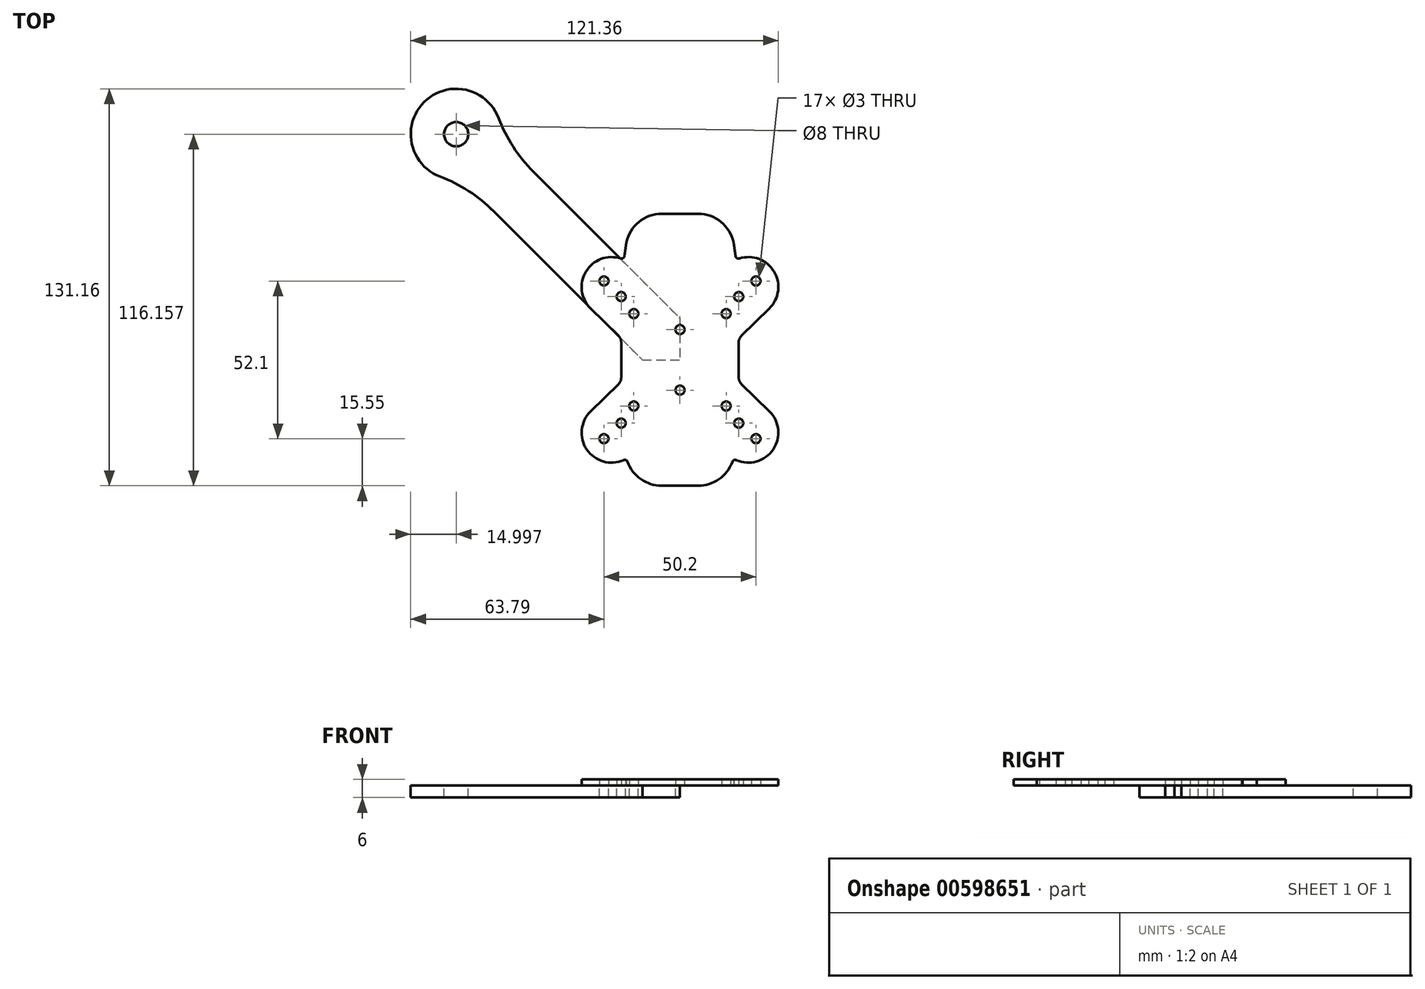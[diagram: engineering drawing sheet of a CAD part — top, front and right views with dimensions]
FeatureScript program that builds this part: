
annotation { "Feature Type Name" : "Feature", "Feature Type Description" : "" }
export const myFeature = defineFeature(function(context is Context, id is Id, definition is map)
    precondition{}
    {
        {
            var Q0;
            Q0=qCreatedBy(makeId("Top.planeOp"),FACE);
            var sketch = newSketch(context, id + "F0", { "sketchPlane" : qUnion([Q0])});
            skLineSegment(sketch, "E0", {"start": v(-6, 48.24) * mm, "end": v(6, 48.24) * mm});
            skLineSegment(sketch, "E1", {"start": v(-6, -41.6) * mm, "end": v(6, -41.6) * mm});
            skCircle(sketch, "E2", {"center": v(-25.1, 26.05) * mm, "radius": 1.5 * mm});
            skCircle(sketch, "E3", {"center": v(-19.4, 20.9) * mm, "radius": 1.5 * mm});
            skCircle(sketch, "E4", {"center": v(-15.25, 15.25) * mm, "radius": 1.5 * mm});
            skCircle(sketch, "E5", {"center": v(0, 10) * mm, "radius": 1.5 * mm});
            skLineSegment(sketch, "E6", {"start": v(-19.4, 5.82) * mm, "end": v(-19.4, -5.82) * mm});
            skCircle(sketch, "E7.MirrorC", {"center": v(-25.1, -26.05) * mm, "radius": 1.5 * mm});
            skCircle(sketch, "E8.MirrorC", {"center": v(-15.25, -15.25) * mm, "radius": 1.5 * mm});
            skCircle(sketch, "E9.MirrorC", {"center": v(-19.4, -20.9) * mm, "radius": 1.5 * mm});
            skCircle(sketch, "E10.MirrorC", {"center": v(0, -10) * mm, "radius": 1.5 * mm});
            skCircle(sketch, "E11.MirrorC", {"center": v(25.1, 26.05) * mm, "radius": 1.5 * mm});
            skCircle(sketch, "E12.MirrorC", {"center": v(19.4, 20.9) * mm, "radius": 1.5 * mm});
            skCircle(sketch, "E13.MirrorC", {"center": v(15.25, 15.25) * mm, "radius": 1.5 * mm});
            skCircle(sketch, "E14.MirrorC", {"center": v(19.4, -20.9) * mm, "radius": 1.5 * mm});
            skCircle(sketch, "E15.MirrorC", {"center": v(15.25, -15.25) * mm, "radius": 1.5 * mm});
            skCircle(sketch, "E16.MirrorC", {"center": v(25.1, -26.05) * mm, "radius": 1.5 * mm});
            skLineSegment(sketch, "E17.MirrorCS", {"start": v(19.4, 5.82) * mm, "end": v(19.4, -5.82) * mm});
            skArc(sketch, "E18", {"start": v(-6, 48.24) * mm, "mid": v(-13.55, 45.57) * mm, "end": v(-17.73, 38.75) * mm});
            skLineSegment(sketch, "E19", {"start": v(-17.74, 38.75) * mm, "end": v(-18.31, 34.31) * mm});
            skArc(sketch, "E20", {"start": v(-19.6, 33.49) * mm, "mid": v(-31.06, 29.17) * mm, "end": v(-29.52, 17.02) * mm});
            skLineSegment(sketch, "E21", {"start": v(-29.52, 17.02) * mm, "end": v(-20.3, 7.97) * mm});
            skArc(sketch, "E22", {"start": v(-19.4, 5.82) * mm, "mid": v(-19.64, 6.98) * mm, "end": v(-20.3, 7.97) * mm});
            skPoint(sketch, "E23.orphan", {"position": v(-19.4, 7.08) * mm});
            skArc(sketch, "E24.MirrorCS", {"start": v(6, 48.24) * mm, "mid": v(13.55, 45.57) * mm, "end": v(17.73, 38.75) * mm});
            skLineSegment(sketch, "E25.MirrorCS", {"start": v(17.74, 38.75) * mm, "end": v(18.31, 34.31) * mm});
            skArc(sketch, "E26.MirrorCS", {"start": v(19.6, 33.49) * mm, "mid": v(31.06, 29.17) * mm, "end": v(29.52, 17.02) * mm});
            skLineSegment(sketch, "E27.MirrorCS", {"start": v(29.52, 17.02) * mm, "end": v(20.3, 7.97) * mm});
            skArc(sketch, "E28.MirrorCS", {"start": v(19.4, 5.82) * mm, "mid": v(19.64, 6.98) * mm, "end": v(20.3, 7.97) * mm});
            skLineSegment(sketch, "E29.MirrorCS", {"start": v(-29.52, -17.02) * mm, "end": v(-20.3, -7.97) * mm});
            skArc(sketch, "E30.MirrorCS", {"start": v(-19.4, -5.82) * mm, "mid": v(-19.64, -6.98) * mm, "end": v(-20.3, -7.97) * mm});
            skLineSegment(sketch, "E31.MirrorCS", {"start": v(29.52, -17.02) * mm, "end": v(20.3, -7.97) * mm});
            skArc(sketch, "E32.MirrorCS", {"start": v(19.4, -5.82) * mm, "mid": v(19.64, -6.98) * mm, "end": v(20.3, -7.97) * mm});
            skArc(sketch, "E33", {"start": v(6, -41.6) * mm, "mid": v(12.89, -39.43) * mm, "end": v(17.28, -33.7) * mm});
            skArc(sketch, "E34", {"start": v(-29.52, -17.02) * mm, "mid": v(-30.78, -29.6) * mm, "end": v(-18.62, -33.12) * mm});
            skArc(sketch, "E35.MirrorC", {"start": v(29.52, -17.02) * mm, "mid": v(30.78, -29.6) * mm, "end": v(18.62, -33.12) * mm});
            skArc(sketch, "E36.MirrorC", {"start": v(-6, -41.6) * mm, "mid": v(-12.89, -39.43) * mm, "end": v(-17.28, -33.7) * mm});
            skPoint(sketch, "E37.visualSharp", {"position": v(-17.62, -32.6) * mm});
            skArc(sketch, "E37.filletArc", {"start": v(-17.28, -33.7) * mm, "mid": v(-17.83, -33.11) * mm, "end": v(-18.62, -33.12) * mm});
            skPoint(sketch, "E38.visualSharp", {"position": v(17.62, -32.6) * mm});
            skArc(sketch, "E38.filletArc", {"start": v(18.62, -33.12) * mm, "mid": v(17.83, -33.11) * mm, "end": v(17.28, -33.7) * mm});
            skPoint(sketch, "E39.visualSharp", {"position": v(18.48, 33.05) * mm});
            skArc(sketch, "E39.filletArc", {"start": v(18.31, 34.31) * mm, "mid": v(18.77, 33.6) * mm, "end": v(19.6, 33.49) * mm});
            skPoint(sketch, "E40.visualSharp", {"position": v(-18.48, 33.05) * mm});
            skArc(sketch, "E40.filletArc", {"start": v(-19.6, 33.49) * mm, "mid": v(-18.77, 33.6) * mm, "end": v(-18.31, 34.31) * mm});
            skSolve(sketch);
        }
        {
            var Q0;
            Q0 = qSketchRegion(id + "F0", true);
            extrude(context, id + "F1", {"entities" : qUnion([Q0]), "depth" : 2 * mm, "offsetDistance" : 25 * mm});
        }
        {
            var Q0;
            Q0=qCreatedBy(makeId("Top.planeOp"),FACE);
            var sketch = newSketch(context, id + "F2", { "sketchPlane" : qUnion([Q0])});
            skLineSegment(sketch, "E41", {"start": v(0, 0.66) * mm, "end": v(-73.9, 74.56) * mm, "construction": true});
            skArc(sketch, "E42", {"start": v(-59.86, 79.86) * mm, "mid": v(-84.5, 85.16) * mm, "end": v(-79.2, 60.53) * mm});
            skLineSegment(sketch, "E43", {"start": v(-48.45, 62.2) * mm, "end": v(0, 13.75) * mm});
            skLineSegment(sketch, "E44", {"start": v(-61.53, 49.12) * mm, "end": v(-12.42, 0) * mm});
            skCircle(sketch, "E45", {"center": v(-25.1, 26.05) * mm, "radius": 1.5 * mm});
            skCircle(sketch, "E46", {"center": v(-15.25, 15.25) * mm, "radius": 1.5 * mm});
            skCircle(sketch, "E47", {"center": v(-19.4, 20.9) * mm, "radius": 1.5 * mm});
            skLineSegment(sketch, "E48", {"start": v(-12.42, 0) * mm, "end": v(0, 0) * mm});
            skLineSegment(sketch, "E49", {"start": v(0, 13.75) * mm, "end": v(0, 11.5) * mm});
            skArc(sketch, "E50", {"start": v(0, 11.5) * mm, "mid": v(-1.5, 10) * mm, "end": v(0, 8.5) * mm});
            skLineSegment(sketch, "E51.trimOffspring", {"start": v(0, 8.5) * mm, "end": v(0, 0.66) * mm});
            skPoint(sketch, "E52.visualSharp", {"position": v(-72.08, 59.67) * mm});
            skArc(sketch, "E52.filletArc", {"start": v(-61.53, 49.12) * mm, "mid": v(-69.76, 55.76) * mm, "end": v(-79.2, 60.53) * mm});
            skPoint(sketch, "E53.visualSharp", {"position": v(-59, 72.75) * mm});
            skArc(sketch, "E53.filletArc", {"start": v(-59.86, 79.86) * mm, "mid": v(-55.1, 70.42) * mm, "end": v(-48.45, 62.2) * mm});
            skLineSegment(sketch, "E54", {"start": v(0, 0.66) * mm, "end": v(0, 0) * mm});
            skCircle(sketch, "E55", {"center": v(-73.9, 74.56) * mm, "radius": 4 * mm});
            skSolve(sketch);
        }
        {
            var Q0;
            Q0=makeQuery(id+"F2.imprint","IMPRINT",FACE,{"disambiguationData":[TD([[makeQuery(id+"F2.imprint","IMPRINT",EDGE,{"derivedFrom":sQuery(id+"F2.wireOp",EDGE,"E42")}),1.0]])]});
            extrude(context, id + "F3", {"entities" : qUnion([Q0]), "oppositeDirection" : true, "depth" : 4 * mm, "offsetDistance" : 25 * mm});
        }
    });
